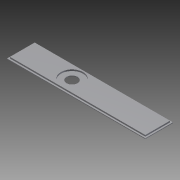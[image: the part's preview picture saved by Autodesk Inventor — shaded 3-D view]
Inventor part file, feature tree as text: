
AUTODESK INVENTOR PART (.ipt)
format: ipt  version: 2011 (Build 150239000, 239)  size: 88,064 bytes
history: native  units: mm
features: extrude x2, sketch x2, other x1
ambient origin geometry x8: Origin, YZ Plane, XZ Plane, XY Plane, X Axis, Y Axis, Z Axis, Center Point
feature tree (5):
  other  "Sólido1"
  extrude  "Extrusión1"  Depth=40.0mm
  extrude  "Extrusión2"  Depth=74.0mm
  sketch  "Boceto1"  dims[d0=200.0mm d1=40.0mm]
  sketch  "Boceto2"  dims[d2=16.0mm d3=74.0mm d4=20.0mm d5=1.0mm d6=0.0mm d7=2.1mm d8=32.0mm d9=2.0mm d10=0.0mm]
